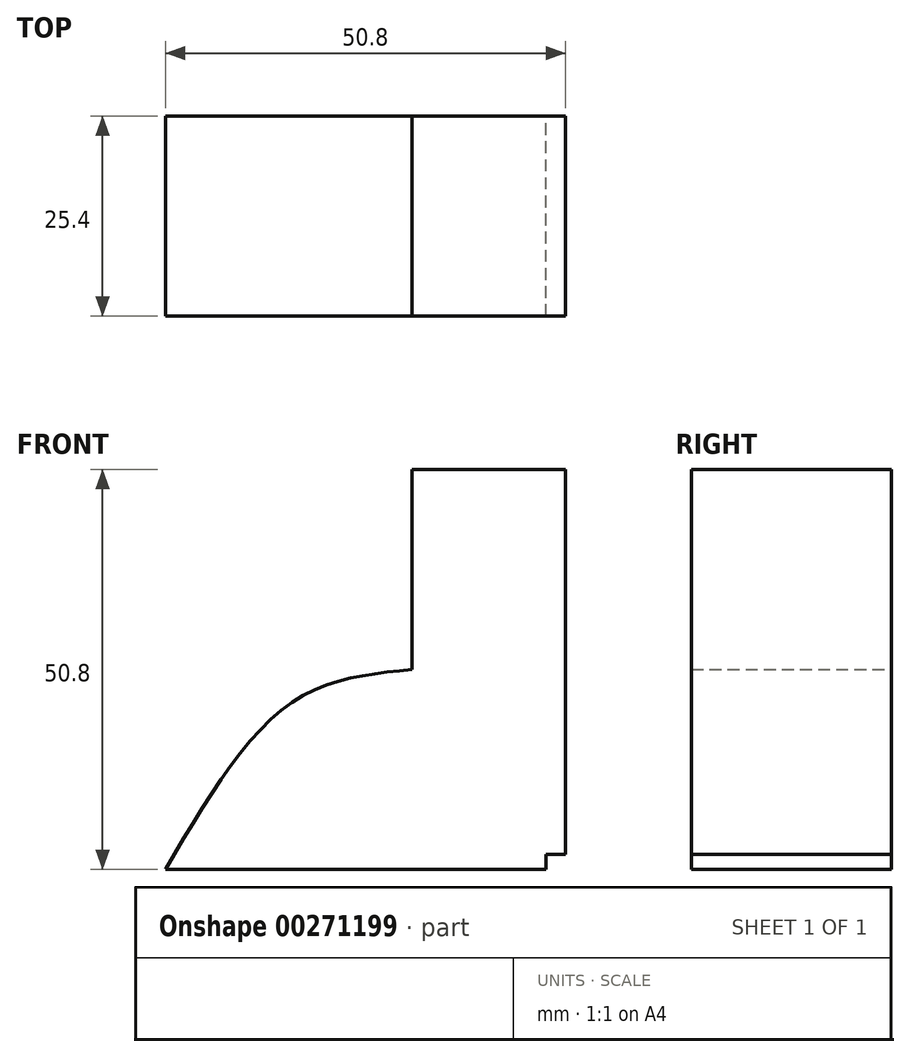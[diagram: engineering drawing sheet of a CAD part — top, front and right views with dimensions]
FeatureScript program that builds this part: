
annotation { "Feature Type Name" : "Feature", "Feature Type Description" : "" }
export const myFeature = defineFeature(function(context is Context, id is Id, definition is map)
    precondition{}
    {
        {
            var Q0;
            Q0=qCreatedBy(makeId("Front.planeOp"),FACE);
            var sketch = newSketch(context, id + "F0", { "sketchPlane" : qUnion([Q0])});
            skLineSegment(sketch, "E0.bottom", {"start": v(0, 0) * mm, "end": v(-2.48, 0) * mm});
            skLineSegment(sketch, "E0.top", {"start": v(0, 1.9) * mm, "end": v(-2.48, 1.9) * mm});
            skLineSegment(sketch, "E0.left", {"start": v(0, 0) * mm, "end": v(0, 1.9) * mm});
            skLineSegment(sketch, "E0.right", {"start": v(-2.48, 0) * mm, "end": v(-2.48, 1.9) * mm});
            skLineSegment(sketch, "E1.bottom", {"start": v(0, 0) * mm, "end": v(-50.8, 0) * mm});
            skLineSegment(sketch, "E1.top", {"start": v(0, 50.8) * mm, "end": v(-50.8, 50.8) * mm});
            skLineSegment(sketch, "E1.left", {"start": v(0, 0) * mm, "end": v(0, 50.8) * mm});
            skLineSegment(sketch, "E1.right", {"start": v(-50.8, 0) * mm, "end": v(-50.8, 50.8) * mm});
            skLineSegment(sketch, "E2", {"start": v(-19.48, 50.8) * mm, "end": v(-19.48, 25.4) * mm});
            skFitSpline(sketch, "E3", {"points": [v(-19.48, 25.4) * mm, v(-34.75, 21.2) * mm, v(-50.8, 0) * mm], "startDerivative": vector(-36.5, -3.57) * mm, "endDerivative": vector(-26.56, -45.43) * mm});
            skSolve(sketch);
        }
        {
            var Q0;
            {var subQ7=sQuery(id+"F0.wireOp",EDGE,"E0.top");Q0=makeQuery(id+"F0.imprint","IMPRINT",FACE,{"disambiguationData":[TD([[makeQuery(id+"F0.imprint","IMPRINT",EDGE,{"derivedFrom":subQ7}),-1.0]])]});}
            extrude(context, id + "F1", {"entities" : qUnion([Q0]), "depth" : 25.4 * mm});
        }
    });
